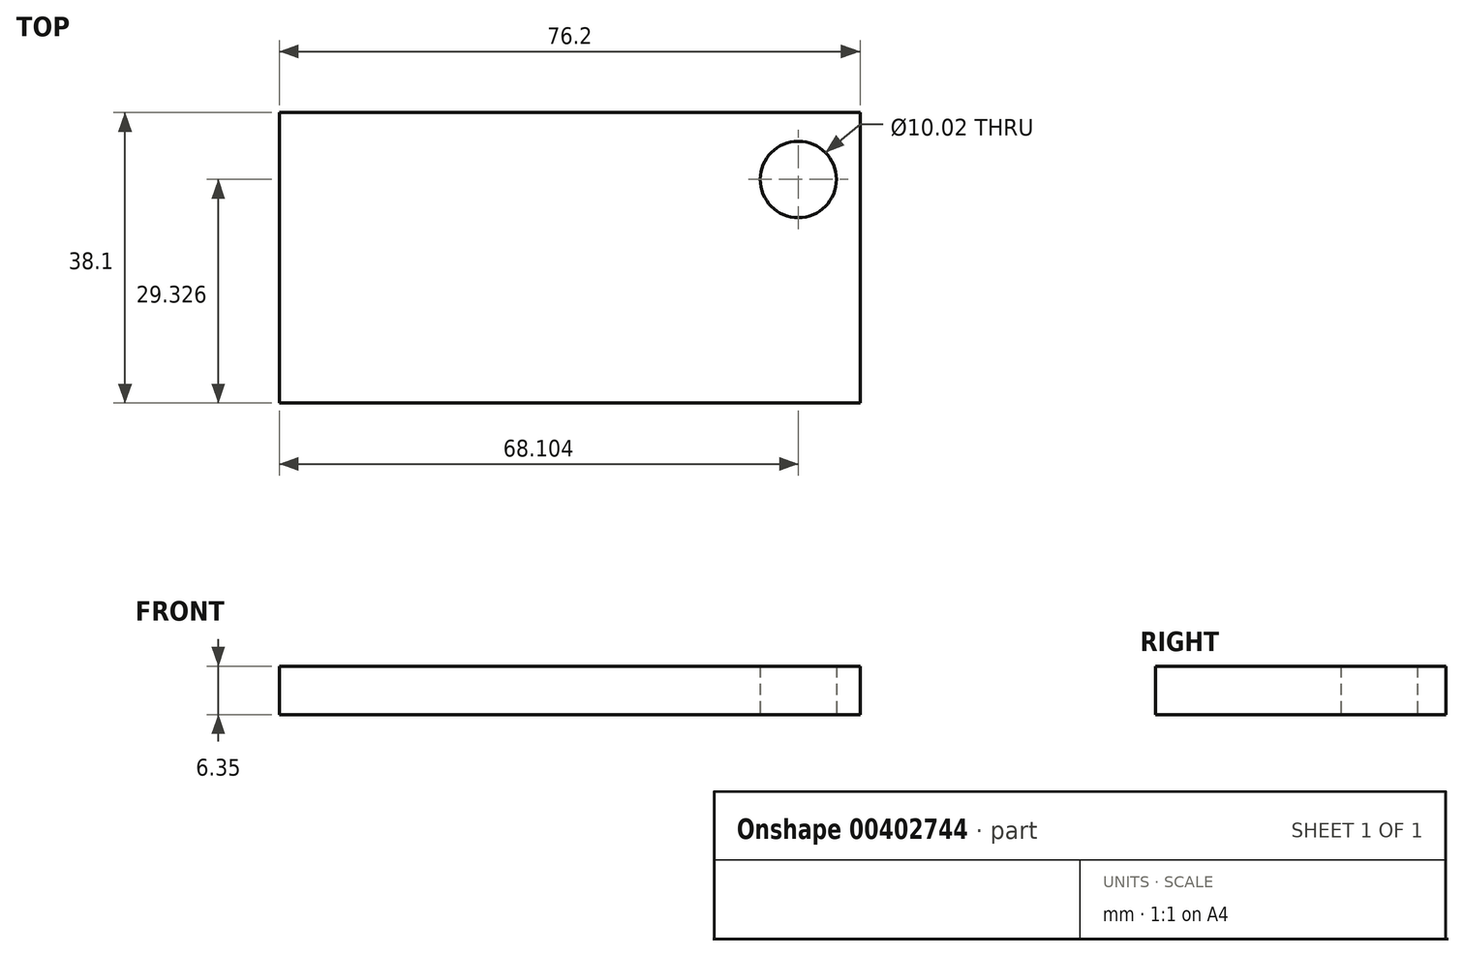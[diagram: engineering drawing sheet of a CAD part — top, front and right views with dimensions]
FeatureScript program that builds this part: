
annotation { "Feature Type Name" : "Feature", "Feature Type Description" : "" }
export const myFeature = defineFeature(function(context is Context, id is Id, definition is map)
    precondition{}
    {
        {
            var Q0;
            Q0=qCreatedBy(makeId("Top.planeOp"),FACE);
            var sketch = newSketch(context, id + "F0", { "sketchPlane" : qUnion([Q0])});
            skLineSegment(sketch, "E0.bottom", {"start": v(-38.1, 19.05) * mm, "end": v(38.1, 19.05) * mm});
            skLineSegment(sketch, "E0.top", {"start": v(-38.1, -19.05) * mm, "end": v(38.1, -19.05) * mm});
            skLineSegment(sketch, "E0.left", {"start": v(-38.1, 19.05) * mm, "end": v(-38.1, -19.05) * mm});
            skLineSegment(sketch, "E0.right", {"start": v(38.1, 19.05) * mm, "end": v(38.1, -19.05) * mm});
            skPoint(sketch, "E0.middle", {"position": v(0, 0) * mm});
            skCircle(sketch, "E1", {"center": v(30, 10.28) * mm, "radius": 5 * mm});
            skSolve(sketch);
        }
        {
            var Q0;
            Q0 = qSketchRegion(id + "F0", true);
            extrude(context, id + "F1", {"entities" : qUnion([Q0]), "depth" : 6.35 * mm});
        }
    });
